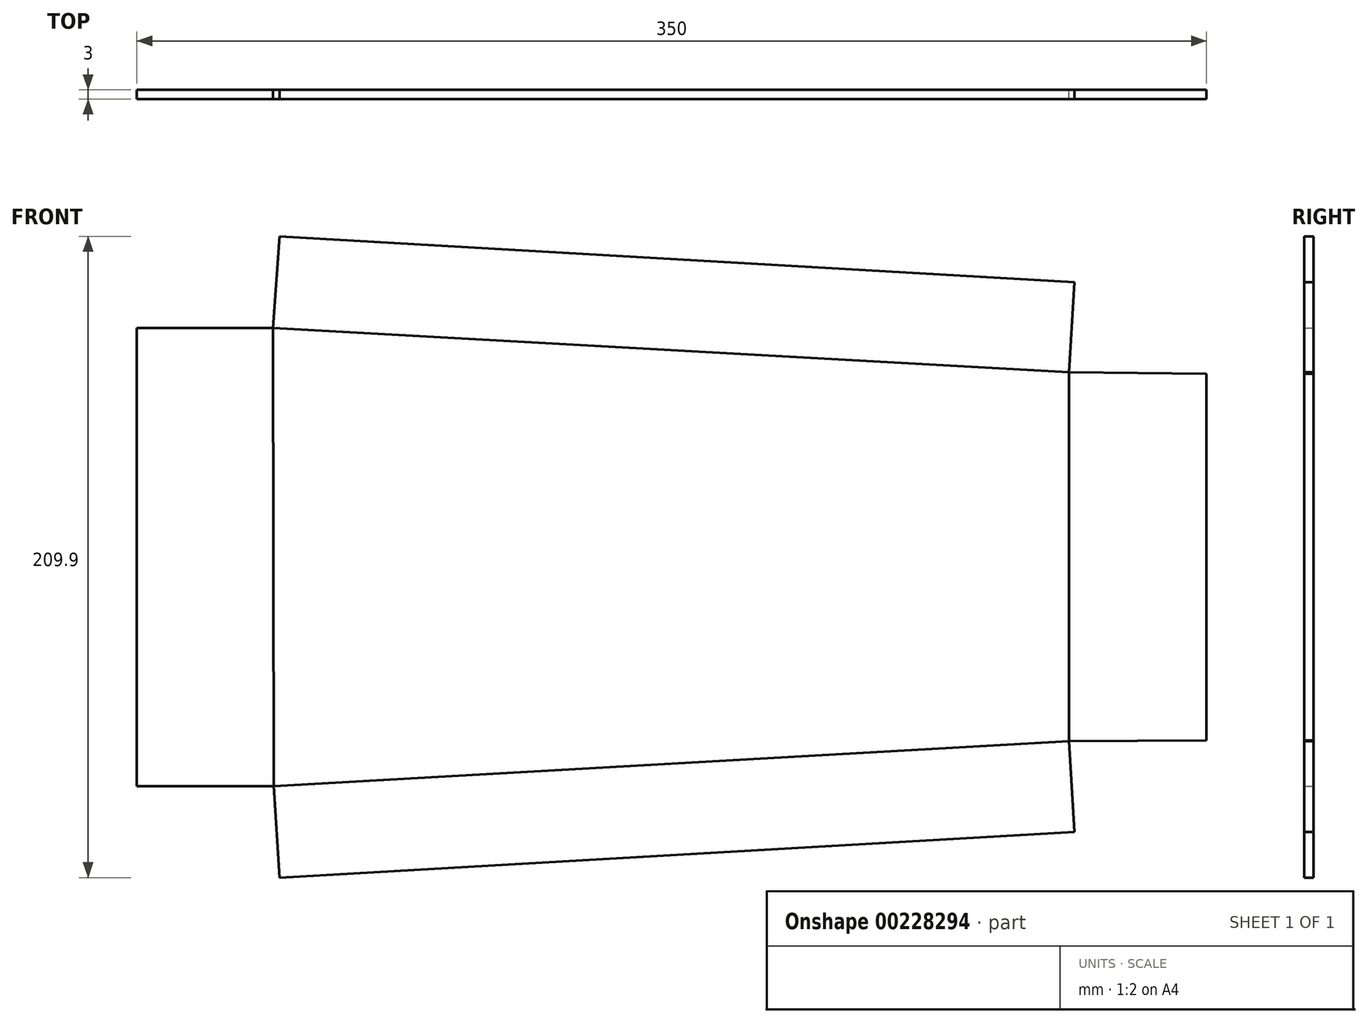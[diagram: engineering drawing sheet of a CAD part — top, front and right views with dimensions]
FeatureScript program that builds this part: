
annotation { "Feature Type Name" : "Feature", "Feature Type Description" : "" }
export const myFeature = defineFeature(function(context is Context, id is Id, definition is map)
    precondition{}
    {
        {
            var Q0;
            Q0=qCreatedBy(makeId("Front.planeOp"),FACE);
            var sketch = newSketch(context, id + "F0", { "sketchPlane" : qUnion([Q0])});
            skLineSegment(sketch, "E0.0", {"start": v(131.73, 89.95) * mm, "end": v(-128.27, 104.95) * mm});
            skLineSegment(sketch, "E1.0", {"start": v(131.73, -89.95) * mm, "end": v(-128.27, -104.95) * mm});
            skLineSegment(sketch, "E2.0", {"start": v(175, -60) * mm, "end": v(175, 60) * mm});
            skLineSegment(sketch, "E3.0", {"start": v(-175, -75) * mm, "end": v(-175, 75) * mm});
            skLineSegment(sketch, "E4", {"start": v(-175, 75) * mm, "end": v(-130.45, 75) * mm});
            skLineSegment(sketch, "E5", {"start": v(-175, -75) * mm, "end": v(-130.3, -75) * mm});
            skLineSegment(sketch, "E6", {"start": v(-130.3, -75) * mm, "end": v(-130.45, 75) * mm});
            skLineSegment(sketch, "E7", {"start": v(-130.3, -75) * mm, "end": v(-128.27, -104.95) * mm});
            skLineSegment(sketch, "E8", {"start": v(131.73, -89.95) * mm, "end": v(130.02, -60.29) * mm});
            skLineSegment(sketch, "E9", {"start": v(130.02, -60.29) * mm, "end": v(-130.3, -75) * mm});
            skLineSegment(sketch, "E10", {"start": v(130.02, -60.29) * mm, "end": v(175, -60) * mm});
            skLineSegment(sketch, "E11", {"start": v(130.02, 60.46) * mm, "end": v(175, 60) * mm});
            skLineSegment(sketch, "E12", {"start": v(130.02, 60.46) * mm, "end": v(130.02, -60.29) * mm});
            skLineSegment(sketch, "E13", {"start": v(-130.45, 75) * mm, "end": v(-128.27, 104.95) * mm});
            skLineSegment(sketch, "E14", {"start": v(-128.27, -104.95) * mm, "end": v(131.73, -89.95) * mm});
            skLineSegment(sketch, "E15", {"start": v(130.02, 60.46) * mm, "end": v(131.73, 89.95) * mm});
            skLineSegment(sketch, "E16", {"start": v(-128.27, 104.95) * mm, "end": v(131.73, 89.95) * mm});
            skLineSegment(sketch, "E17", {"start": v(130.02, 60.46) * mm, "end": v(-130.45, 75) * mm});
            skSolve(sketch);
        }
        {
            var Q0;
            Q0=makeQuery(id+"F0.imprint","IMPRINT",FACE,{"disambiguationData":[TD([[makeQuery(id+"F0.imprint","IMPRINT",EDGE,{"derivedFrom":sQuery(id+"F0.wireOp",EDGE,"E13")}),-1.0]])]});
            var Q1;
            Q1=makeQuery(id+"F0.imprint","IMPRINT",FACE,{"disambiguationData":[TD([[makeQuery(id+"F0.imprint","IMPRINT",EDGE,{"derivedFrom":sQuery(id+"F0.wireOp",EDGE,"E3.0")}),-1.0]])]});
            var Q2;
            Q2=makeQuery(id+"F0.imprint","IMPRINT",FACE,{"disambiguationData":[TD([[makeQuery(id+"F0.imprint","IMPRINT",EDGE,{"derivedFrom":sQuery(id+"F0.wireOp",EDGE,"E7")}),1.0]])]});
            var Q3;
            Q3=makeQuery(id+"F0.imprint","IMPRINT",FACE,{"disambiguationData":[TD([[makeQuery(id+"F0.imprint","IMPRINT",EDGE,{"derivedFrom":sQuery(id+"F0.wireOp",EDGE,"E2.0")}),1.0]])]});
            extrude(context, id + "F1", {"entities" : qUnion([Q0, Q1, Q2, Q3]), "depth" : 3 * mm});
        }
    });
